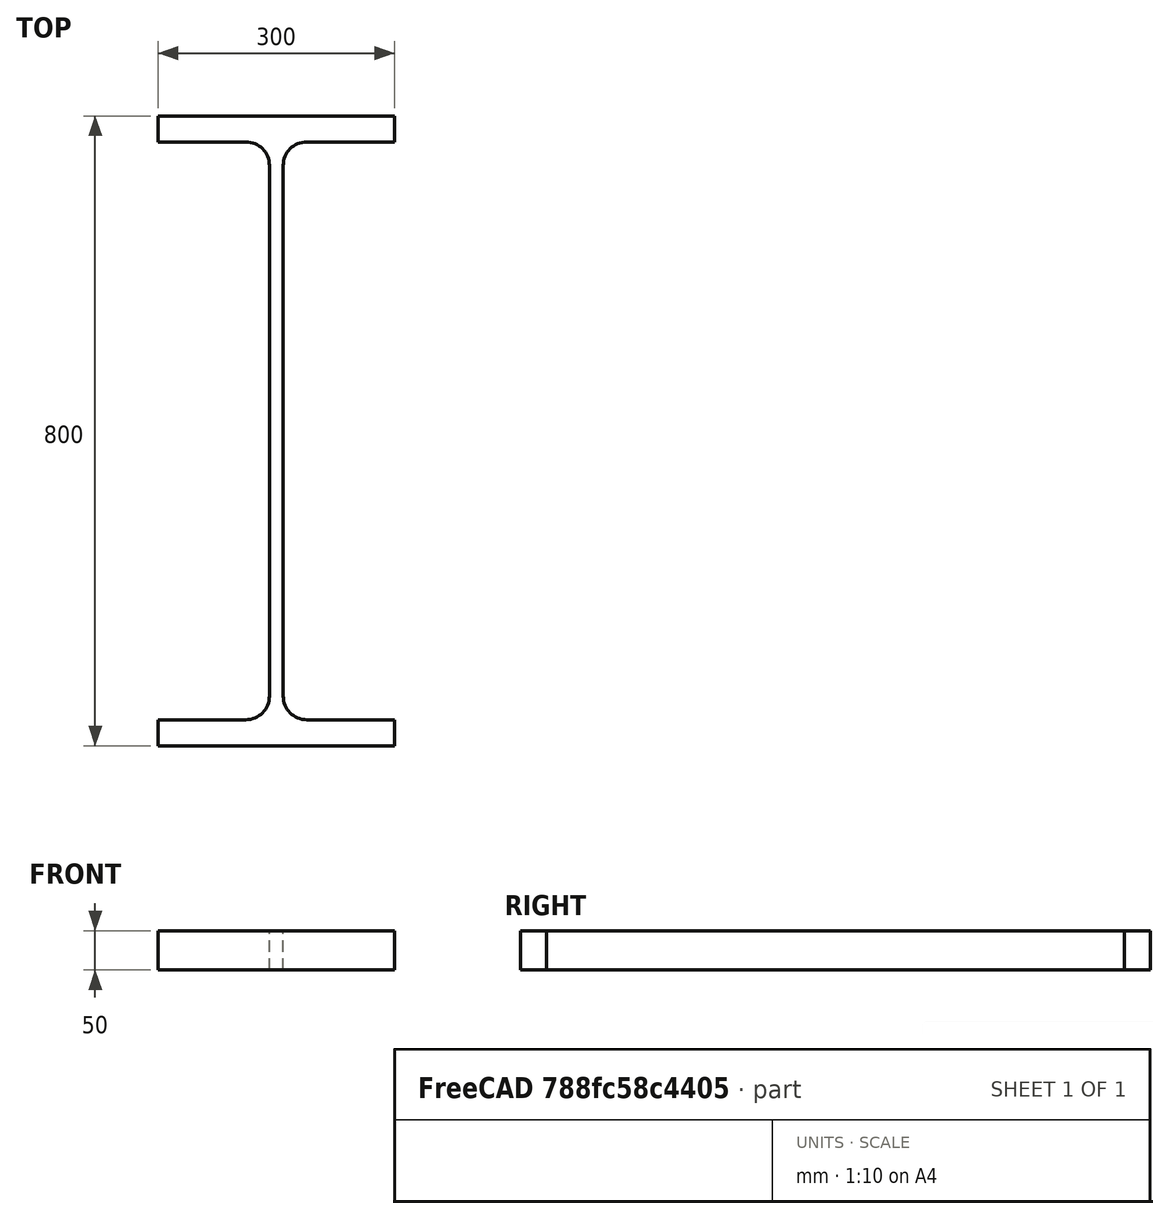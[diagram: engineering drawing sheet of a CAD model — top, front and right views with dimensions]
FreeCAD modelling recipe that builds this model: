
FCSTD DOCUMENT  (FreeCAD 0.15R4671 (Git))
Label: HE-B-Profile 800 DIN1025-2 S235JR
License: All rights reserved
LicenseURL: http://en.wikipedia.org/wiki/All_rights_reserved
objects: Sketcher::SketchObject×1, Part::Extrusion×1
note: 2 computed .brp shape members not serialized (recipe doc carries the construction recipe); baked Part::Feature solids carry a one-line shape summary decoded from their .brp

FEATURE [Sketcher::SketchObject] Sketch
  sketch-geometry (16):
    g0: LineSegment StartX=8.75 StartY=-337 StartZ=0 EndX=8.75 EndY=337 EndZ=0
    g1: LineSegment StartX=38.75 StartY=367 StartZ=0 EndX=150 EndY=367 EndZ=0
    g2: LineSegment StartX=150 StartY=367 StartZ=0 EndX=150 EndY=400 EndZ=0
    g3: LineSegment StartX=150 StartY=400 StartZ=0 EndX=-150 EndY=400 EndZ=0
    g4: LineSegment StartX=-150 StartY=400 StartZ=0 EndX=-150 EndY=367 EndZ=0
    g5: LineSegment StartX=-150 StartY=367 StartZ=0 EndX=-38.75 EndY=367 EndZ=0
    g6: LineSegment StartX=-8.75 StartY=337 StartZ=0 EndX=-8.75 EndY=-337 EndZ=0
    g7: LineSegment StartX=-38.75 StartY=-367 StartZ=0 EndX=-150 EndY=-367 EndZ=0
    g8: LineSegment StartX=-150 StartY=-367 StartZ=0 EndX=-150 EndY=-400 EndZ=0
    g9: LineSegment StartX=-150 StartY=-400 StartZ=0 EndX=150 EndY=-400 EndZ=0
    g10: LineSegment StartX=150 StartY=-400 StartZ=0 EndX=150 EndY=-367 EndZ=0
    g11: LineSegment StartX=150 StartY=-367 StartZ=0 EndX=38.75 EndY=-367 EndZ=0
    g12: ArcOfCircle CenterX=38.75 CenterY=337 CenterZ=0 NormalX=0 NormalY=0 NormalZ=1 Radius=30 StartAngle=1.5708 EndAngle=3.14159
    g13: ArcOfCircle CenterX=38.75 CenterY=-337 CenterZ=0 NormalX=0 NormalY=0 NormalZ=1 Radius=30 StartAngle=3.14159 EndAngle=4.71239
    g14: ArcOfCircle CenterX=-38.75 CenterY=337 CenterZ=0 NormalX=0 NormalY=0 NormalZ=1 Radius=30 StartAngle=0 EndAngle=1.5708
    g15: ArcOfCircle CenterX=-38.75 CenterY=-337 CenterZ=0 NormalX=0 NormalY=0 NormalZ=1 Radius=30 StartAngle=4.71239 EndAngle=6.28319
  constraints (42):
    c: Vertical(g0)
    c: Coincident(g2,g1)
    c: Vertical(g2)
    c: Coincident(g3,g2)
    c: Coincident(g4,g3)
    c: Vertical(g4)
    c: Coincident(g5,g4)
    c: Horizontal(g5)
    c: Vertical(g6)
    c: Horizontal(g7)
    c: Coincident(g8,g7)
    c: Vertical(g8)
    c: Coincident(g9,g8)
    c: Horizontal(g9)
    c: Coincident(g10,g9)
    c: Vertical(g10)
    c: Coincident(g11,g10)
    c: Horizontal(g11)
    c: Tangent(g1,g12) = 1.5708
    c: Tangent(g0,g12) = 1.5708
    c: Tangent(g0,g13) = 1.5708
    c: Tangent(g11,g13) = 1.5708
    c: Tangent(g5,g14) = 1.5708
    c: Tangent(g6,g14) = 1.5708
    c: Tangent(g6,g15) = 1.5708
    c: Tangent(g7,g15) = 1.5708
    c: Equal(g3,g9)
    c: Equal(g2,g4)
    c: Equal(g4,g8)
    c: Equal(g8,g10)
    c: Equal(g12,g14)
    c: Equal(g14,g15)
    c: Equal(g15,g13)
    c: Symmetric(g2,g3,g-2)
    c: Symmetric(g9,g8,g-2)
    c: Symmetric(g0,g6,g-2)
    c: Symmetric(g2,g9,g-1)
    c: DistanceY(g2,g9) = -800
    c: DistanceX(g3) = -300
    c: DistanceX(g0,g6) = -17.5
    c: DistanceY(g2) = 33
    c: Radius(g12) = 30
FEATURE [Part::Extrusion] Extrude  label="HE-B-Profile 800 DIN1025-2 S235JR"
  Base = -> Sketch
  Dir = (0,0,50)
  Solid = true
